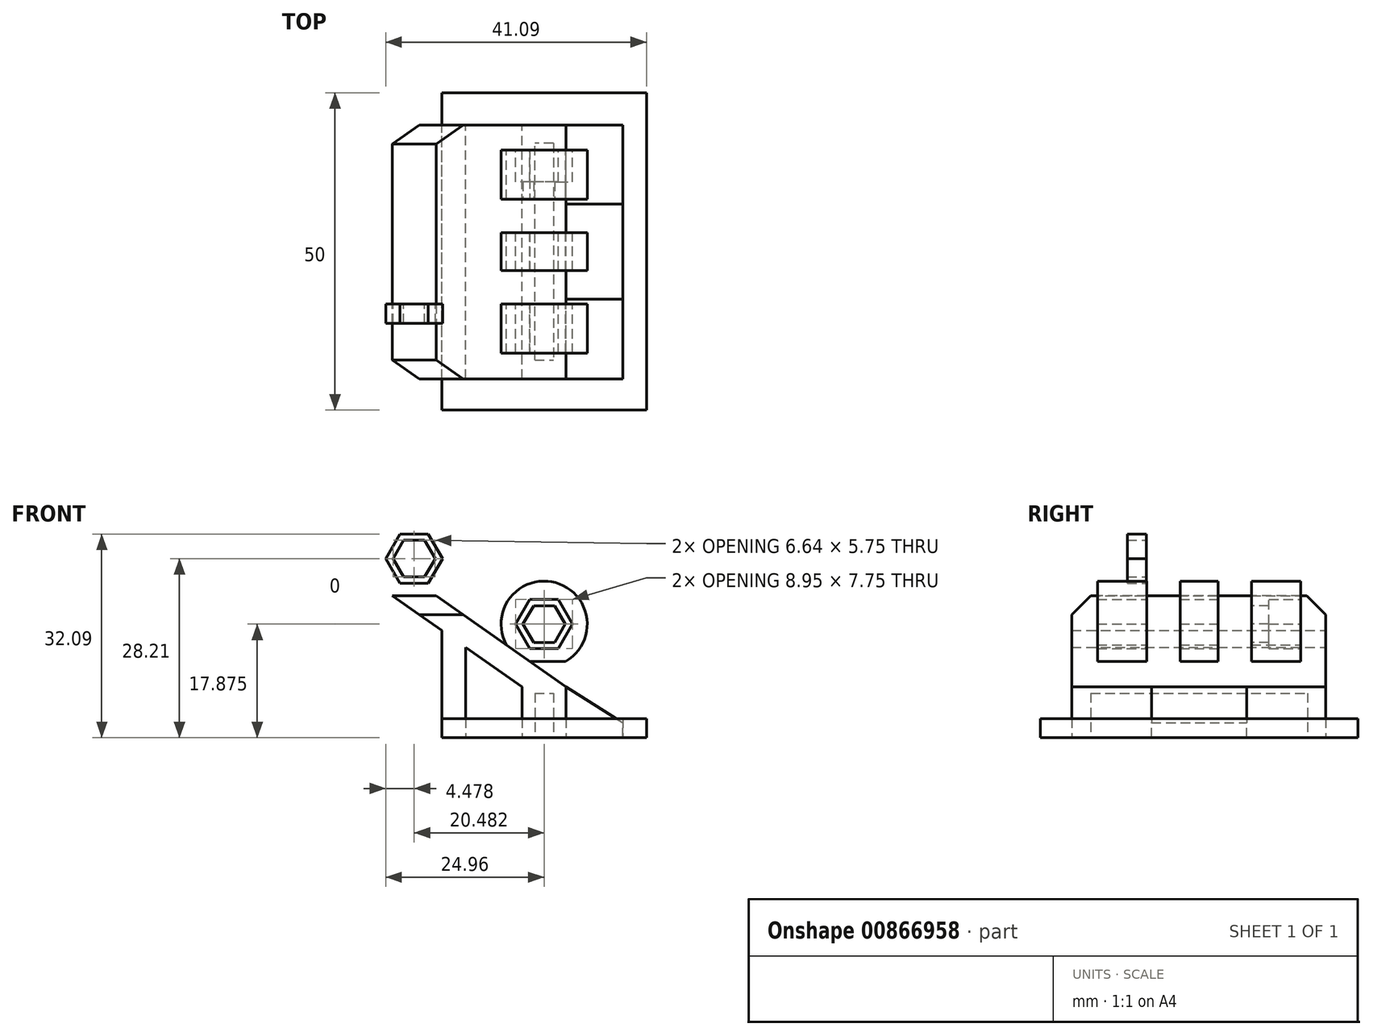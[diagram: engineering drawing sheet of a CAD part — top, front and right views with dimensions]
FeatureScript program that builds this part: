
annotation { "Feature Type Name" : "Feature", "Feature Type Description" : "" }
export const myFeature = defineFeature(function(context is Context, id is Id, definition is map)
    precondition{}
    {
        {
            var Q0;
            Q0=qCreatedBy(makeId("Top.planeOp"),FACE);
            var sketch = newSketch(context, id + "F0", { "sketchPlane" : qUnion([Q0])});
            skLineSegment(sketch, "E0.bottom", {"start": v(16.12, -25) * mm, "end": v(-16.13, -25) * mm});
            skLineSegment(sketch, "E0.top", {"start": v(16.12, 25) * mm, "end": v(-16.12, 25) * mm});
            skLineSegment(sketch, "E0.left", {"start": v(16.12, -25) * mm, "end": v(16.12, 25) * mm});
            skLineSegment(sketch, "E0.right", {"start": v(-16.13, -25) * mm, "end": v(-16.12, 25) * mm});
            skPoint(sketch, "E0.middle", {"position": v(0, 0) * mm});
            skLineSegment(sketch, "E1", {"start": v(12.38, -25) * mm, "end": v(12.38, 25) * mm});
            skLineSegment(sketch, "E2", {"start": v(-12.38, -25) * mm, "end": v(-12.38, 25) * mm});
            skLineSegment(sketch, "E3", {"start": v(12.38, -20.07) * mm, "end": v(-12.38, -20.07) * mm});
            skLineSegment(sketch, "E4.MirrorCS", {"start": v(12.38, 19.93) * mm, "end": v(-12.38, 19.93) * mm});
            skLineSegment(sketch, "E5", {"start": v(-3.46, 0) * mm, "end": v(3.46, 0) * mm});
            skLineSegment(sketch, "E6", {"start": v(-3.46, -20.07) * mm, "end": v(-3.46, 19.93) * mm});
            skLineSegment(sketch, "E7", {"start": v(3.46, 19.93) * mm, "end": v(3.46, -20.07) * mm});
            skLineSegment(sketch, "E8", {"start": v(-3.46, -20.07) * mm, "end": v(-1.47, -17.07) * mm});
            skLineSegment(sketch, "E9.MirrorCS", {"start": v(-3.46, 20.07) * mm, "end": v(-1.47, 17.07) * mm});
            skLineSegment(sketch, "E10.MirrorCS", {"start": v(3.46, -20.07) * mm, "end": v(1.47, -17.07) * mm});
            skLineSegment(sketch, "E11.MirrorCS", {"start": v(3.46, 20.07) * mm, "end": v(1.47, 17.07) * mm});
            skLineSegment(sketch, "E12", {"start": v(-1.47, -17.07) * mm, "end": v(1.47, -17.07) * mm});
            skLineSegment(sketch, "E13", {"start": v(1.47, 17.07) * mm, "end": v(1.47, -17.07) * mm});
            skLineSegment(sketch, "E14", {"start": v(-1.47, -17.07) * mm, "end": v(-1.47, 17.07) * mm});
            skLineSegment(sketch, "E15", {"start": v(1.47, 17.07) * mm, "end": v(-1.47, 17.07) * mm});
            skLineSegment(sketch, "E16", {"start": v(-12.38, 19.93) * mm, "end": v(-16.12, 19.93) * mm});
            skLineSegment(sketch, "E17", {"start": v(-12.38, -20.07) * mm, "end": v(-16.13, -20.07) * mm});
            skSolve(sketch);
        }
        {
            var Q0;
            {var subQ0=sQuery(id+"F0.wireOp",EDGE,"E0.left");Q0=makeQuery(id+"F0.imprint","IMPRINT",FACE,{"disambiguationData":[TD([[makeQuery(id+"F0.imprint","IMPRINT",EDGE,{"derivedFrom":subQ0}),1.0]])]});}
            var Q1;
            {var subQ1=sQuery(id+"F0.wireOp",EDGE,"E1");var subQ4=sQuery(id+"F0.wireOp",EDGE,"E0.bottom");var subQ5=makeQuery(id+"F0.imprint","INTERSECT",VERTEX,{"derivedFrom":[subQ4,subQ1]});Q1=makeQuery(id+"F0.imprint","IMPRINT",FACE,{"disambiguationData":[TD([[makeQuery(id+"F0.imprint","IMPRINT",EDGE,{"disambiguationData":[TD([[subQ5,-1.0]])],"derivedFrom":subQ4}),-1.0]])]});}
            var Q2;
            {var subQ1=sQuery(id+"F0.wireOp",EDGE,"E1");var subQ5=sQuery(id+"F0.wireOp",EDGE,"E0.top");var subQ8=makeQuery(id+"F0.imprint","INTERSECT",VERTEX,{"derivedFrom":[subQ5,subQ1]});Q2=makeQuery(id+"F0.imprint","IMPRINT",FACE,{"disambiguationData":[TD([[makeQuery(id+"F0.imprint","IMPRINT",EDGE,{"disambiguationData":[TD([[subQ8,-1.0]])],"derivedFrom":subQ5}),1.0]])]});}
            var Q3;
            {var subQ5=sQuery(id+"F0.wireOp",EDGE,"E17");Q3=makeQuery(id+"F0.imprint","IMPRINT",FACE,{"disambiguationData":[TD([[makeQuery(id+"F0.imprint","IMPRINT",EDGE,{"derivedFrom":subQ5}),1.0]])]});}
            var Q4;
            {var subQ5=sQuery(id+"F0.wireOp",EDGE,"E16");Q4=makeQuery(id+"F0.imprint","IMPRINT",FACE,{"disambiguationData":[TD([[makeQuery(id+"F0.imprint","IMPRINT",EDGE,{"derivedFrom":subQ5}),-1.0]])]});}
            extrude(context, id + "F1", {"entities" : qUnion([Q0, Q1, Q2, Q3, Q4]), "depth" : 3 * mm, "offsetDistance" : 25 * mm});
        }
        {
            var Q0;
            {var subQ5=sQuery(id+"F0.wireOp",EDGE,"E8");Q0=makeQuery(id+"F0.imprint","IMPRINT",FACE,{"disambiguationData":[TD([[makeQuery(id+"F0.imprint","IMPRINT",EDGE,{"derivedFrom":subQ5}),1.0]])]});}
            var Q1;
            {var subQ0=sQuery(id+"F0.wireOp",EDGE,"E6");var subQ3=sQuery(id+"F0.wireOp",EDGE,"E4.MirrorCS");var subQ4=makeQuery(id+"F0.imprint","INTERSECT",VERTEX,{"derivedFrom":[subQ3,subQ0]});Q1=makeQuery(id+"F0.imprint","IMPRINT",FACE,{"disambiguationData":[TD([[makeQuery(id+"F0.imprint","IMPRINT",EDGE,{"disambiguationData":[TD([[subQ4,1.0]])],"derivedFrom":subQ3}),1.0]])]});}
            var Q2;
            {var subQ5=sQuery(id+"F0.wireOp",EDGE,"E15");Q2=makeQuery(id+"F0.imprint","IMPRINT",FACE,{"disambiguationData":[TD([[makeQuery(id+"F0.imprint","IMPRINT",EDGE,{"derivedFrom":subQ5}),-1.0]])]});}
            var Q3;
            {var subQ5=sQuery(id+"F0.wireOp",EDGE,"E15");Q3=makeQuery(id+"F0.imprint","IMPRINT",FACE,{"disambiguationData":[TD([[makeQuery(id+"F0.imprint","IMPRINT",EDGE,{"derivedFrom":subQ5}),1.0]])]});}
            var Q4;
            {var subQ0=sQuery(id+"F0.wireOp",EDGE,"E8");Q4=makeQuery(id+"F0.imprint","IMPRINT",FACE,{"disambiguationData":[TD([[makeQuery(id+"F0.imprint","IMPRINT",EDGE,{"derivedFrom":subQ0}),-1.0]])]});}
            var Q5;
            {var subQ5=sQuery(id+"F0.wireOp",EDGE,"E10.MirrorCS");Q5=makeQuery(id+"F0.imprint","IMPRINT",FACE,{"disambiguationData":[TD([[makeQuery(id+"F0.imprint","IMPRINT",EDGE,{"derivedFrom":subQ5}),-1.0]])]});}
            var Q6;
            {var subQ3=sQuery(id+"F0.wireOp",EDGE,"E4.MirrorCS");var subQ5=sQuery(id+"F0.wireOp",EDGE,"E7");var subQ8=makeQuery(id+"F0.imprint","INTERSECT",VERTEX,{"derivedFrom":[subQ3,subQ5]});Q6=makeQuery(id+"F0.imprint","IMPRINT",FACE,{"disambiguationData":[TD([[makeQuery(id+"F0.imprint","IMPRINT",EDGE,{"disambiguationData":[TD([[subQ8,-1.0]])],"derivedFrom":subQ3}),1.0]])]});}
            var Q7;
            {var subQ5=sQuery(id+"F0.wireOp",EDGE,"E12");Q7=makeQuery(id+"F0.imprint","IMPRINT",FACE,{"disambiguationData":[TD([[makeQuery(id+"F0.imprint","IMPRINT",EDGE,{"derivedFrom":subQ5}),1.0]])]});}
            extrude(context, id + "F2", {"entities" : qUnion([Q0, Q1, Q2, Q3, Q4, Q5, Q6, Q7]), "operationType" : NewBodyOperationType.ADD, "depth" : 8 * mm, "offsetDistance" : 25 * mm});
        }
        {
            var Q0;
            {var subQ5=sQuery(id+"F0.wireOp",EDGE,"E12");Q0=makeQuery(id+"F0.imprint","IMPRINT",FACE,{"disambiguationData":[TD([[makeQuery(id+"F0.imprint","IMPRINT",EDGE,{"derivedFrom":subQ5}),1.0]])]});}
            var Q1;
            {var subQ5=sQuery(id+"F0.wireOp",EDGE,"E15");Q1=makeQuery(id+"F0.imprint","IMPRINT",FACE,{"disambiguationData":[TD([[makeQuery(id+"F0.imprint","IMPRINT",EDGE,{"derivedFrom":subQ5}),1.0]])]});}
            extrude(context, id + "F3", {"entities" : qUnion([Q0, Q1]), "operationType" : NewBodyOperationType.REMOVE, "depth" : 7 * mm, "offsetDistance" : 25 * mm});
        }
        {
            var Q0;
            Q0=qCreatedBy(makeId("Front.planeOp"),FACE);
            var sketch = newSketch(context, id + "F4", { "sketchPlane" : qUnion([Q0])});
            skLineSegment(sketch, "E18", {"start": v(0, 0) * mm, "end": v(0, 11.88) * mm});
            skLineSegment(sketch, "E19", {"start": v(0, 11.88) * mm, "end": v(0, 23.88) * mm});
            skCircle(sketch, "E20", {"center": v(0, 17.88) * mm, "radius": 3.88 * mm});
            skCircle(sketch, "E21.cCircle", {"center": v(0, 17.88) * mm, "radius": 3.88 * mm, "construction": true});
            skLineSegment(sketch, "E21.0", {"start": v(2.24, 14) * mm, "end": v(-2.24, 14) * mm});
            skLineSegment(sketch, "E21.1", {"start": v(-2.24, 14) * mm, "end": v(-4.47, 17.88) * mm});
            skLineSegment(sketch, "E21.2", {"start": v(-4.47, 17.88) * mm, "end": v(-2.24, 21.75) * mm});
            skLineSegment(sketch, "E21.3", {"start": v(-2.24, 21.75) * mm, "end": v(2.24, 21.75) * mm});
            skLineSegment(sketch, "E21.4", {"start": v(2.24, 21.75) * mm, "end": v(4.47, 17.88) * mm});
            skLineSegment(sketch, "E21.5", {"start": v(4.47, 17.88) * mm, "end": v(2.24, 14) * mm});
            skPoint(sketch, "E21.0.midPoint", {"position": v(0, 14) * mm});
            skLineSegment(sketch, "E22.0", {"start": v(-6.78, 17.88) * mm, "end": v(-3.4, 23.75) * mm});
            skLineSegment(sketch, "E22.1", {"start": v(3.4, 23.75) * mm, "end": v(6.78, 17.88) * mm});
            skLineSegment(sketch, "E22.2", {"start": v(6.78, 17.88) * mm, "end": v(3.4, 12) * mm});
            skLineSegment(sketch, "E22.3", {"start": v(-3.4, 23.75) * mm, "end": v(3.4, 23.75) * mm});
            skLineSegment(sketch, "E22.4", {"start": v(3.4, 12) * mm, "end": v(-3.4, 12) * mm});
            skLineSegment(sketch, "E22.5", {"start": v(-3.4, 12) * mm, "end": v(-6.78, 17.88) * mm});
            skLineSegment(sketch, "E23.0", {"start": v(-1.66, 20.75) * mm, "end": v(1.66, 20.75) * mm});
            skLineSegment(sketch, "E23.1", {"start": v(3.32, 17.88) * mm, "end": v(1.66, 15) * mm});
            skLineSegment(sketch, "E23.2", {"start": v(1.66, 15) * mm, "end": v(-1.66, 15) * mm});
            skLineSegment(sketch, "E23.3", {"start": v(1.66, 20.75) * mm, "end": v(3.32, 17.88) * mm});
            skLineSegment(sketch, "E23.4", {"start": v(-1.66, 15) * mm, "end": v(-3.32, 17.88) * mm});
            skLineSegment(sketch, "E23.5", {"start": v(-3.32, 17.88) * mm, "end": v(-1.66, 20.75) * mm});
            skCircle(sketch, "E24", {"center": v(0, 17.88) * mm, "radius": 6.78 * mm});
            skSolve(sketch);
        }
        {
            var Q0;
            {var subQ1=sQuery(id+"F4.wireOp",EDGE,"E22.1");Q0=makeQuery(id+"F4.imprint","IMPRINT",FACE,{"disambiguationData":[TD([[makeQuery(id+"F4.imprint","IMPRINT",EDGE,{"derivedFrom":subQ1}),-1.0]])]});}
            var Q1;
            {var subQ14=sQuery(id+"F4.wireOp",EDGE,"E22.0");Q1=makeQuery(id+"F4.imprint","IMPRINT",FACE,{"disambiguationData":[TD([[makeQuery(id+"F4.imprint","IMPRINT",EDGE,{"derivedFrom":subQ14}),-1.0]])]});}
            var Q2;
            {var subQ0=sQuery(id+"F4.wireOp",EDGE,"E22.0");Q2=makeQuery(id+"F4.imprint","IMPRINT",FACE,{"disambiguationData":[TD([[makeQuery(id+"F4.imprint","IMPRINT",EDGE,{"derivedFrom":subQ0}),1.0]])]});}
            var Q3;
            {var subQ0=sQuery(id+"F4.wireOp",EDGE,"E22.5");Q3=makeQuery(id+"F4.imprint","IMPRINT",FACE,{"disambiguationData":[TD([[makeQuery(id+"F4.imprint","IMPRINT",EDGE,{"derivedFrom":subQ0}),1.0]])]});}
            var Q4;
            {var subQ0=sQuery(id+"F4.wireOp",EDGE,"E22.2");Q4=makeQuery(id+"F4.imprint","IMPRINT",FACE,{"disambiguationData":[TD([[makeQuery(id+"F4.imprint","IMPRINT",EDGE,{"derivedFrom":subQ0}),1.0]])]});}
            var Q5;
            {var subQ0=sQuery(id+"F4.wireOp",EDGE,"E22.1");Q5=makeQuery(id+"F4.imprint","IMPRINT",FACE,{"disambiguationData":[TD([[makeQuery(id+"F4.imprint","IMPRINT",EDGE,{"derivedFrom":subQ0}),1.0]])]});}
            var Q6;
            {var subQ0=sQuery(id+"F4.wireOp",EDGE,"E22.3");var subQ1=makeQuery(id+"F4.imprint","INTERSECT",VERTEX,{"derivedFrom":[sQuery(id+"F4.wireOp",EDGE,"E19"),subQ0]});Q6=makeQuery(id+"F4.imprint","IMPRINT",FACE,{"disambiguationData":[TD([[makeQuery(id+"F4.imprint","IMPRINT",EDGE,{"disambiguationData":[TD([[subQ1,1.0]])],"derivedFrom":subQ0}),1.0]])]});}
            extrude(context, id + "F5", {"entities" : qUnion([Q0, Q1, Q2, Q3, Q4, Q5, Q6]), "operationType" : NewBodyOperationType.ADD, "depth" : 16 * mm, "offsetDistance" : 25 * mm, "hasSecondDirection" : true, "secondDirectionOppositeDirection" : true, "secondDirectionDepth" : 16 * mm});
        }
        {
            var Q0;
            {var subQ0=sQuery(id+"F4.wireOp",EDGE,"E21.2");var subQ1=sQuery(id+"F4.wireOp",EDGE,"E20");var subQ2=makeQuery(id+"F4.imprint","INTERSECT",VERTEX,{"derivedFrom":[subQ1,subQ0]});Q0=makeQuery(id+"F4.imprint","IMPRINT",FACE,{"disambiguationData":[TD([[makeQuery(id+"F4.imprint","IMPRINT",EDGE,{"disambiguationData":[TD([[subQ2,-1.0]])],"derivedFrom":subQ1}),-1.0]])]});}
            var Q1;
            {var subQ0=sQuery(id+"F4.wireOp",EDGE,"E21.2");var subQ3=sQuery(id+"F4.wireOp",EDGE,"E21.3");var subQ5=makeQuery(id+"F4.imprint","INTERSECT",VERTEX,{"derivedFrom":[subQ0,subQ3]});Q1=makeQuery(id+"F4.imprint","IMPRINT",FACE,{"disambiguationData":[TD([[makeQuery(id+"F4.imprint","IMPRINT",EDGE,{"disambiguationData":[TD([[subQ5,1.0]])],"derivedFrom":subQ0}),-1.0]])]});}
            var Q2;
            {var subQ11=sQuery(id+"F4.wireOp",EDGE,"E23.4");Q2=makeQuery(id+"F4.imprint","IMPRINT",FACE,{"disambiguationData":[TD([[makeQuery(id+"F4.imprint","IMPRINT",EDGE,{"derivedFrom":subQ11}),1.0]])]});}
            var Q3;
            {var subQ11=sQuery(id+"F4.wireOp",EDGE,"E23.1");Q3=makeQuery(id+"F4.imprint","IMPRINT",FACE,{"disambiguationData":[TD([[makeQuery(id+"F4.imprint","IMPRINT",EDGE,{"derivedFrom":subQ11}),1.0]])]});}
            var Q4;
            {var subQ0=sQuery(id+"F4.wireOp",EDGE,"E21.4");var subQ3=sQuery(id+"F4.wireOp",EDGE,"E21.3");var subQ5=makeQuery(id+"F4.imprint","INTERSECT",VERTEX,{"derivedFrom":[subQ3,subQ0]});Q4=makeQuery(id+"F4.imprint","IMPRINT",FACE,{"disambiguationData":[TD([[makeQuery(id+"F4.imprint","IMPRINT",EDGE,{"disambiguationData":[TD([[subQ5,-1.0]])],"derivedFrom":subQ0}),-1.0]])]});}
            var Q5;
            {var subQ0=sQuery(id+"F4.wireOp",EDGE,"E21.4");var subQ1=sQuery(id+"F4.wireOp",EDGE,"E20");var subQ2=makeQuery(id+"F4.imprint","INTERSECT",VERTEX,{"derivedFrom":[subQ1,subQ0]});Q5=makeQuery(id+"F4.imprint","IMPRINT",FACE,{"disambiguationData":[TD([[makeQuery(id+"F4.imprint","IMPRINT",EDGE,{"disambiguationData":[TD([[subQ2,1.0]])],"derivedFrom":subQ1}),-1.0]])]});}
            var Q6;
            {var subQ0=sQuery(id+"F4.wireOp",EDGE,"E21.5");var subQ3=sQuery(id+"F4.wireOp",EDGE,"E21.0");var subQ5=makeQuery(id+"F4.imprint","INTERSECT",VERTEX,{"derivedFrom":[subQ3,subQ0]});Q6=makeQuery(id+"F4.imprint","IMPRINT",FACE,{"disambiguationData":[TD([[makeQuery(id+"F4.imprint","IMPRINT",EDGE,{"disambiguationData":[TD([[subQ5,1.0]])],"derivedFrom":subQ0}),-1.0]])]});}
            var Q7;
            {var subQ0=sQuery(id+"F4.wireOp",EDGE,"E21.1");var subQ3=sQuery(id+"F4.wireOp",EDGE,"E21.0");var subQ5=makeQuery(id+"F4.imprint","INTERSECT",VERTEX,{"derivedFrom":[subQ3,subQ0]});Q7=makeQuery(id+"F4.imprint","IMPRINT",FACE,{"disambiguationData":[TD([[makeQuery(id+"F4.imprint","IMPRINT",EDGE,{"disambiguationData":[TD([[subQ5,-1.0]])],"derivedFrom":subQ0}),-1.0]])]});}
            extrude(context, id + "F6", {"entities" : qUnion([Q0, Q1, Q2, Q3, Q4, Q5, Q6, Q7]), "depth" : (16 - 4.7) * mm, "offsetDistance" : 25 * mm, "hasSecondDirection" : true, "secondDirectionOppositeDirection" : false, "secondDirectionDepth" : 8.3 * mm});
        }
        {
            var Q0;
            {var subQ0=sQuery(id+"F4.wireOp",EDGE,"E21.4");var subQ3=sQuery(id+"F4.wireOp",EDGE,"E21.3");var subQ5=makeQuery(id+"F4.imprint","INTERSECT",VERTEX,{"derivedFrom":[subQ3,subQ0]});Q0=makeQuery(id+"F4.imprint","IMPRINT",FACE,{"disambiguationData":[TD([[makeQuery(id+"F4.imprint","IMPRINT",EDGE,{"disambiguationData":[TD([[subQ5,-1.0]])],"derivedFrom":subQ0}),-1.0]])]});}
            var Q1;
            {var subQ11=sQuery(id+"F4.wireOp",EDGE,"E23.1");Q1=makeQuery(id+"F4.imprint","IMPRINT",FACE,{"disambiguationData":[TD([[makeQuery(id+"F4.imprint","IMPRINT",EDGE,{"derivedFrom":subQ11}),1.0]])]});}
            var Q2;
            {var subQ11=sQuery(id+"F4.wireOp",EDGE,"E23.4");Q2=makeQuery(id+"F4.imprint","IMPRINT",FACE,{"disambiguationData":[TD([[makeQuery(id+"F4.imprint","IMPRINT",EDGE,{"derivedFrom":subQ11}),1.0]])]});}
            var Q3;
            {var subQ0=sQuery(id+"F4.wireOp",EDGE,"E21.2");var subQ3=sQuery(id+"F4.wireOp",EDGE,"E21.3");var subQ5=makeQuery(id+"F4.imprint","INTERSECT",VERTEX,{"derivedFrom":[subQ0,subQ3]});Q3=makeQuery(id+"F4.imprint","IMPRINT",FACE,{"disambiguationData":[TD([[makeQuery(id+"F4.imprint","IMPRINT",EDGE,{"disambiguationData":[TD([[subQ5,1.0]])],"derivedFrom":subQ0}),-1.0]])]});}
            var Q4;
            {var subQ0=sQuery(id+"F4.wireOp",EDGE,"E21.4");var subQ1=sQuery(id+"F4.wireOp",EDGE,"E20");var subQ2=makeQuery(id+"F4.imprint","INTERSECT",VERTEX,{"derivedFrom":[subQ1,subQ0]});Q4=makeQuery(id+"F4.imprint","IMPRINT",FACE,{"disambiguationData":[TD([[makeQuery(id+"F4.imprint","IMPRINT",EDGE,{"disambiguationData":[TD([[subQ2,1.0]])],"derivedFrom":subQ1}),-1.0]])]});}
            var Q5;
            {var subQ0=sQuery(id+"F4.wireOp",EDGE,"E21.5");var subQ3=sQuery(id+"F4.wireOp",EDGE,"E21.0");var subQ5=makeQuery(id+"F4.imprint","INTERSECT",VERTEX,{"derivedFrom":[subQ3,subQ0]});Q5=makeQuery(id+"F4.imprint","IMPRINT",FACE,{"disambiguationData":[TD([[makeQuery(id+"F4.imprint","IMPRINT",EDGE,{"disambiguationData":[TD([[subQ5,1.0]])],"derivedFrom":subQ0}),-1.0]])]});}
            var Q6;
            {var subQ0=sQuery(id+"F4.wireOp",EDGE,"E21.1");var subQ3=sQuery(id+"F4.wireOp",EDGE,"E21.0");var subQ5=makeQuery(id+"F4.imprint","INTERSECT",VERTEX,{"derivedFrom":[subQ3,subQ0]});Q6=makeQuery(id+"F4.imprint","IMPRINT",FACE,{"disambiguationData":[TD([[makeQuery(id+"F4.imprint","IMPRINT",EDGE,{"disambiguationData":[TD([[subQ5,-1.0]])],"derivedFrom":subQ0}),-1.0]])]});}
            var Q7;
            {var subQ0=sQuery(id+"F4.wireOp",EDGE,"E21.2");var subQ1=sQuery(id+"F4.wireOp",EDGE,"E20");var subQ2=makeQuery(id+"F4.imprint","INTERSECT",VERTEX,{"derivedFrom":[subQ1,subQ0]});Q7=makeQuery(id+"F4.imprint","IMPRINT",FACE,{"disambiguationData":[TD([[makeQuery(id+"F4.imprint","IMPRINT",EDGE,{"disambiguationData":[TD([[subQ2,-1.0]])],"derivedFrom":subQ1}),-1.0]])]});}
            extrude(context, id + "F7", {"entities" : qUnion([Q0, Q1, Q2, Q3, Q4, Q5, Q6, Q7]), "operationType" : NewBodyOperationType.ADD, "oppositeDirection" : true, "depth" : (16 - 5) * mm, "offsetDistance" : 25 * mm, "hasSecondDirection" : true, "secondDirectionOppositeDirection" : true, "secondDirectionDepth" : 8.25 * mm});
        }
        {
            var Q0;
            {var subQ0=sQuery(id+"F4.wireOp",EDGE,"E22.0");Q0=makeQuery(id+"F4.imprint","IMPRINT",FACE,{"disambiguationData":[TD([[makeQuery(id+"F4.imprint","IMPRINT",EDGE,{"derivedFrom":subQ0}),1.0]])]});}
            var Q1;
            {var subQ14=sQuery(id+"F4.wireOp",EDGE,"E22.0");Q1=makeQuery(id+"F4.imprint","IMPRINT",FACE,{"disambiguationData":[TD([[makeQuery(id+"F4.imprint","IMPRINT",EDGE,{"derivedFrom":subQ14}),-1.0]])]});}
            var Q2;
            {var subQ1=sQuery(id+"F4.wireOp",EDGE,"E22.1");Q2=makeQuery(id+"F4.imprint","IMPRINT",FACE,{"disambiguationData":[TD([[makeQuery(id+"F4.imprint","IMPRINT",EDGE,{"derivedFrom":subQ1}),-1.0]])]});}
            var Q3;
            {var subQ0=sQuery(id+"F4.wireOp",EDGE,"E22.3");var subQ1=makeQuery(id+"F4.imprint","INTERSECT",VERTEX,{"derivedFrom":[sQuery(id+"F4.wireOp",EDGE,"E19"),subQ0]});Q3=makeQuery(id+"F4.imprint","IMPRINT",FACE,{"disambiguationData":[TD([[makeQuery(id+"F4.imprint","IMPRINT",EDGE,{"disambiguationData":[TD([[subQ1,1.0]])],"derivedFrom":subQ0}),1.0]])]});}
            var Q4;
            {var subQ0=sQuery(id+"F4.wireOp",EDGE,"E22.1");Q4=makeQuery(id+"F4.imprint","IMPRINT",FACE,{"disambiguationData":[TD([[makeQuery(id+"F4.imprint","IMPRINT",EDGE,{"derivedFrom":subQ0}),1.0]])]});}
            var Q5;
            {var subQ0=sQuery(id+"F4.wireOp",EDGE,"E22.5");Q5=makeQuery(id+"F4.imprint","IMPRINT",FACE,{"disambiguationData":[TD([[makeQuery(id+"F4.imprint","IMPRINT",EDGE,{"derivedFrom":subQ0}),1.0]])]});}
            var Q6;
            {var subQ0=sQuery(id+"F4.wireOp",EDGE,"E22.2");Q6=makeQuery(id+"F4.imprint","IMPRINT",FACE,{"disambiguationData":[TD([[makeQuery(id+"F4.imprint","IMPRINT",EDGE,{"derivedFrom":subQ0}),1.0]])]});}
            extrude(context, id + "F8", {"entities" : qUnion([Q0, Q1, Q2, Q3, Q4, Q5, Q6]), "operationType" : NewBodyOperationType.REMOVE, "oppositeDirection" : true, "depth" : 8.25 * mm, "offsetDistance" : 25 * mm, "hasSecondDirection" : true, "secondDirectionOppositeDirection" : true, "secondDirectionDepth" : 3 * mm});
        }
        {
            var Q0;
            {var subQ1=sQuery(id+"F4.wireOp",EDGE,"E22.1");Q0=makeQuery(id+"F4.imprint","IMPRINT",FACE,{"disambiguationData":[TD([[makeQuery(id+"F4.imprint","IMPRINT",EDGE,{"derivedFrom":subQ1}),-1.0]])]});}
            var Q1;
            {var subQ0=sQuery(id+"F4.wireOp",EDGE,"E22.3");var subQ1=makeQuery(id+"F4.imprint","INTERSECT",VERTEX,{"derivedFrom":[sQuery(id+"F4.wireOp",EDGE,"E19"),subQ0]});Q1=makeQuery(id+"F4.imprint","IMPRINT",FACE,{"disambiguationData":[TD([[makeQuery(id+"F4.imprint","IMPRINT",EDGE,{"disambiguationData":[TD([[subQ1,1.0]])],"derivedFrom":subQ0}),1.0]])]});}
            var Q2;
            {var subQ14=sQuery(id+"F4.wireOp",EDGE,"E22.0");Q2=makeQuery(id+"F4.imprint","IMPRINT",FACE,{"disambiguationData":[TD([[makeQuery(id+"F4.imprint","IMPRINT",EDGE,{"derivedFrom":subQ14}),-1.0]])]});}
            var Q3;
            {var subQ0=sQuery(id+"F4.wireOp",EDGE,"E22.1");Q3=makeQuery(id+"F4.imprint","IMPRINT",FACE,{"disambiguationData":[TD([[makeQuery(id+"F4.imprint","IMPRINT",EDGE,{"derivedFrom":subQ0}),1.0]])]});}
            var Q4;
            {var subQ0=sQuery(id+"F4.wireOp",EDGE,"E22.2");Q4=makeQuery(id+"F4.imprint","IMPRINT",FACE,{"disambiguationData":[TD([[makeQuery(id+"F4.imprint","IMPRINT",EDGE,{"derivedFrom":subQ0}),1.0]])]});}
            var Q5;
            {var subQ0=sQuery(id+"F4.wireOp",EDGE,"E22.0");Q5=makeQuery(id+"F4.imprint","IMPRINT",FACE,{"disambiguationData":[TD([[makeQuery(id+"F4.imprint","IMPRINT",EDGE,{"derivedFrom":subQ0}),1.0]])]});}
            var Q6;
            {var subQ0=sQuery(id+"F4.wireOp",EDGE,"E22.5");Q6=makeQuery(id+"F4.imprint","IMPRINT",FACE,{"disambiguationData":[TD([[makeQuery(id+"F4.imprint","IMPRINT",EDGE,{"derivedFrom":subQ0}),1.0]])]});}
            extrude(context, id + "F9", {"entities" : qUnion([Q0, Q1, Q2, Q3, Q4, Q5, Q6]), "operationType" : NewBodyOperationType.REMOVE, "depth" : 8.25 * mm, "offsetDistance" : 25 * mm, "hasSecondDirection" : true, "secondDirectionOppositeDirection" : false, "secondDirectionDepth" : 3 * mm});
        }
        {
            var Q0;
            Q0=qCreatedBy(makeId("Front.planeOp"),FACE);
            var sketch = newSketch(context, id + "F10", { "sketchPlane" : qUnion([Q0])});
            skLineSegment(sketch, "E25", {"start": v(0, 0) * mm, "end": v(0, 8) * mm});
            skLineSegment(sketch, "E26", {"start": v(0, 8) * mm, "end": v(-3.47, 8) * mm});
            skLineSegment(sketch, "E27", {"start": v(-3.47, 8) * mm, "end": v(-23.95, 22.33) * mm});
            skLineSegment(sketch, "E28", {"start": v(-23.95, 22.33) * mm, "end": v(-23.95, 8) * mm});
            skLineSegment(sketch, "E29", {"start": v(-23.95, 8) * mm, "end": v(-3.47, 8) * mm});
            skLineSegment(sketch, "E30", {"start": v(0, 0) * mm, "end": v(-16.12, 0) * mm});
            skLineSegment(sketch, "E31", {"start": v(0, 0) * mm, "end": v(16.12, 0) * mm});
            skLineSegment(sketch, "E32", {"start": v(0, -2.3) * mm, "end": v(3.46, -2.3) * mm});
            skLineSegment(sketch, "E33", {"start": v(3.46, -2.3) * mm, "end": v(3.46, 0) * mm});
            skLineSegment(sketch, "E34", {"start": v(3.46, 0) * mm, "end": v(3.46, 8) * mm});
            skLineSegment(sketch, "E35", {"start": v(3.46, 8) * mm, "end": v(16.12, 0) * mm});
            skSolve(sketch);
        }
        {
            var Q0;
            Q0=makeQuery(id+"F2.opExtrude","CAP_FACE",FACE,{"disambiguationData":[OSD([sQuery(id+"F0.wireOp",EDGE,"E3"),sQuery(id+"F0.wireOp",EDGE,"E4.MirrorCS"),sQuery(id+"F0.wireOp",EDGE,"E6"),sQuery(id+"F0.wireOp",EDGE,"E7")])],"isStart":false});
            var Q1;
            Q1=sQuery(id+"F10.wireOp",EDGE,"E27");
            sweep(context, id + "F11", {"operationType" : NewBodyOperationType.ADD, "profiles" : qUnion([Q0]), "path" : qUnion([Q1])});
        }
        {
            var Q0;
            Q0=makeQuery(id+"F8.boolean.opBoolean","SPLIT",BODY,{"disambiguationData":[OD(0.0)],"derivedFrom":makeQuery(id+"F5.opExtrude","SWEPT_BODY",BODY,{"disambiguationData":[OSD([sQuery(id+"F4.wireOp",EDGE,"E21.0"),sQuery(id+"F4.wireOp",EDGE,"E21.1"),sQuery(id+"F4.wireOp",EDGE,"E21.2"),sQuery(id+"F4.wireOp",EDGE,"E21.3"),sQuery(id+"F4.wireOp",EDGE,"E21.4"),sQuery(id+"F4.wireOp",EDGE,"E21.5"),sQuery(id+"F4.wireOp",EDGE,"E22.4"),sQuery(id+"F4.wireOp",EDGE,"E24")])]})});
            var Q1;
            Q1=makeQuery(id+"F9.boolean.opBoolean","SPLIT",BODY,{"disambiguationData":[OD(0.0)],"derivedFrom":makeQuery(id+"F8.boolean.opBoolean","SPLIT",BODY,{"disambiguationData":[OD(1.0)],"derivedFrom":makeQuery(id+"F5.opExtrude","SWEPT_BODY",BODY,{"disambiguationData":[OSD([sQuery(id+"F4.wireOp",EDGE,"E21.0"),sQuery(id+"F4.wireOp",EDGE,"E21.1"),sQuery(id+"F4.wireOp",EDGE,"E21.2"),sQuery(id+"F4.wireOp",EDGE,"E21.3"),sQuery(id+"F4.wireOp",EDGE,"E21.4"),sQuery(id+"F4.wireOp",EDGE,"E21.5"),sQuery(id+"F4.wireOp",EDGE,"E22.4"),sQuery(id+"F4.wireOp",EDGE,"E24")])]})})});
            var Q2;
            Q2=makeQuery(id+"F9.boolean.opBoolean","SPLIT",BODY,{"disambiguationData":[OD(1.0)],"derivedFrom":makeQuery(id+"F8.boolean.opBoolean","SPLIT",BODY,{"disambiguationData":[OD(1.0)],"derivedFrom":makeQuery(id+"F5.opExtrude","SWEPT_BODY",BODY,{"disambiguationData":[OSD([sQuery(id+"F4.wireOp",EDGE,"E21.0"),sQuery(id+"F4.wireOp",EDGE,"E21.1"),sQuery(id+"F4.wireOp",EDGE,"E21.2"),sQuery(id+"F4.wireOp",EDGE,"E21.3"),sQuery(id+"F4.wireOp",EDGE,"E21.4"),sQuery(id+"F4.wireOp",EDGE,"E21.5"),sQuery(id+"F4.wireOp",EDGE,"E22.4"),sQuery(id+"F4.wireOp",EDGE,"E24")])]})})});
            var Q3;
            Q3=makeQuery(id+"F7.opExtrude","SWEPT_BODY",BODY,{"disambiguationData":[OSD([sQuery(id+"F4.wireOp",EDGE,"E21.0"),sQuery(id+"F4.wireOp",EDGE,"E21.1"),sQuery(id+"F4.wireOp",EDGE,"E21.2"),sQuery(id+"F4.wireOp",EDGE,"E21.3"),sQuery(id+"F4.wireOp",EDGE,"E21.4"),sQuery(id+"F4.wireOp",EDGE,"E21.5"),sQuery(id+"F4.wireOp",EDGE,"E23.0"),sQuery(id+"F4.wireOp",EDGE,"E23.1"),sQuery(id+"F4.wireOp",EDGE,"E23.2"),sQuery(id+"F4.wireOp",EDGE,"E23.3"),sQuery(id+"F4.wireOp",EDGE,"E23.4"),sQuery(id+"F4.wireOp",EDGE,"E23.5")])]});
            var Q4;
            Q4=makeQuery(id+"F6.opExtrude","SWEPT_BODY",BODY,{"disambiguationData":[OSD([sQuery(id+"F4.wireOp",EDGE,"E21.0"),sQuery(id+"F4.wireOp",EDGE,"E21.1"),sQuery(id+"F4.wireOp",EDGE,"E21.2"),sQuery(id+"F4.wireOp",EDGE,"E21.3"),sQuery(id+"F4.wireOp",EDGE,"E21.4"),sQuery(id+"F4.wireOp",EDGE,"E21.5"),sQuery(id+"F4.wireOp",EDGE,"E23.0"),sQuery(id+"F4.wireOp",EDGE,"E23.1"),sQuery(id+"F4.wireOp",EDGE,"E23.2"),sQuery(id+"F4.wireOp",EDGE,"E23.3"),sQuery(id+"F4.wireOp",EDGE,"E23.4"),sQuery(id+"F4.wireOp",EDGE,"E23.5")])]});
            transform(context, id + "F12", {"entities" : qUnion([Q0, Q1, Q2, Q3, Q4]), "transformType" : TransformType.TRANSLATION_3D, "dx" : -20.48 * mm, "dy" : 0 * mm, "dz" : 10.34 * mm, "makeCopy" : false});
        }
        {
            var Q0;
            {var subQ0=sQuery(id+"F0.wireOp",EDGE,"E16");Q0=makeQuery(id+"F0.imprint","IMPRINT",FACE,{"disambiguationData":[TD([[makeQuery(id+"F0.imprint","IMPRINT",EDGE,{"derivedFrom":subQ0}),1.0]])]});}
            extrude(context, id + "F13", {"entities" : qUnion([Q0]), "operationType" : NewBodyOperationType.ADD, "depth" : 16.86 * mm, "offsetDistance" : 25 * mm});
        }
        {
            var Q0;
            {var subQ0=sQuery(id+"F10.wireOp",EDGE,"E35");Q0=makeQuery(id+"F10.imprint","IMPRINT",FACE,{"disambiguationData":[TD([[makeQuery(id+"F10.imprint","IMPRINT",EDGE,{"derivedFrom":subQ0}),-1.0]])]});}
            extrude(context, id + "F14", {"entities" : qUnion([Q0]), "operationType" : NewBodyOperationType.ADD, "depth" : 7.5 * mm, "offsetDistance" : 25 * mm, "hasSecondDirection" : true, "secondDirectionOppositeDirection" : true, "secondDirectionDepth" : 7.5 * mm});
        }
        {
            var Q0;
            Q0=makeQuery(id+"F11.opSweep","CAP_EDGE",EDGE,{"disambiguationData":[OSD([sQuery(id+"F0.wireOp",EDGE,"E3"),sQuery(id+"F10.wireOp",VERTEX,"E27.end")])],"isStart":false});
            var Q1;
            Q1=makeQuery(id+"F11.opSweep","CAP_EDGE",EDGE,{"disambiguationData":[OSD([sQuery(id+"F0.wireOp",EDGE,"E4.MirrorCS"),sQuery(id+"F10.wireOp",VERTEX,"E27.end")])],"isStart":false});
            chamfer(context, id + "F15", {"entities" : qUnion([Q0, Q1]), "width" : 3 * mm, "tangentPropagation" : true});
        }
    });
